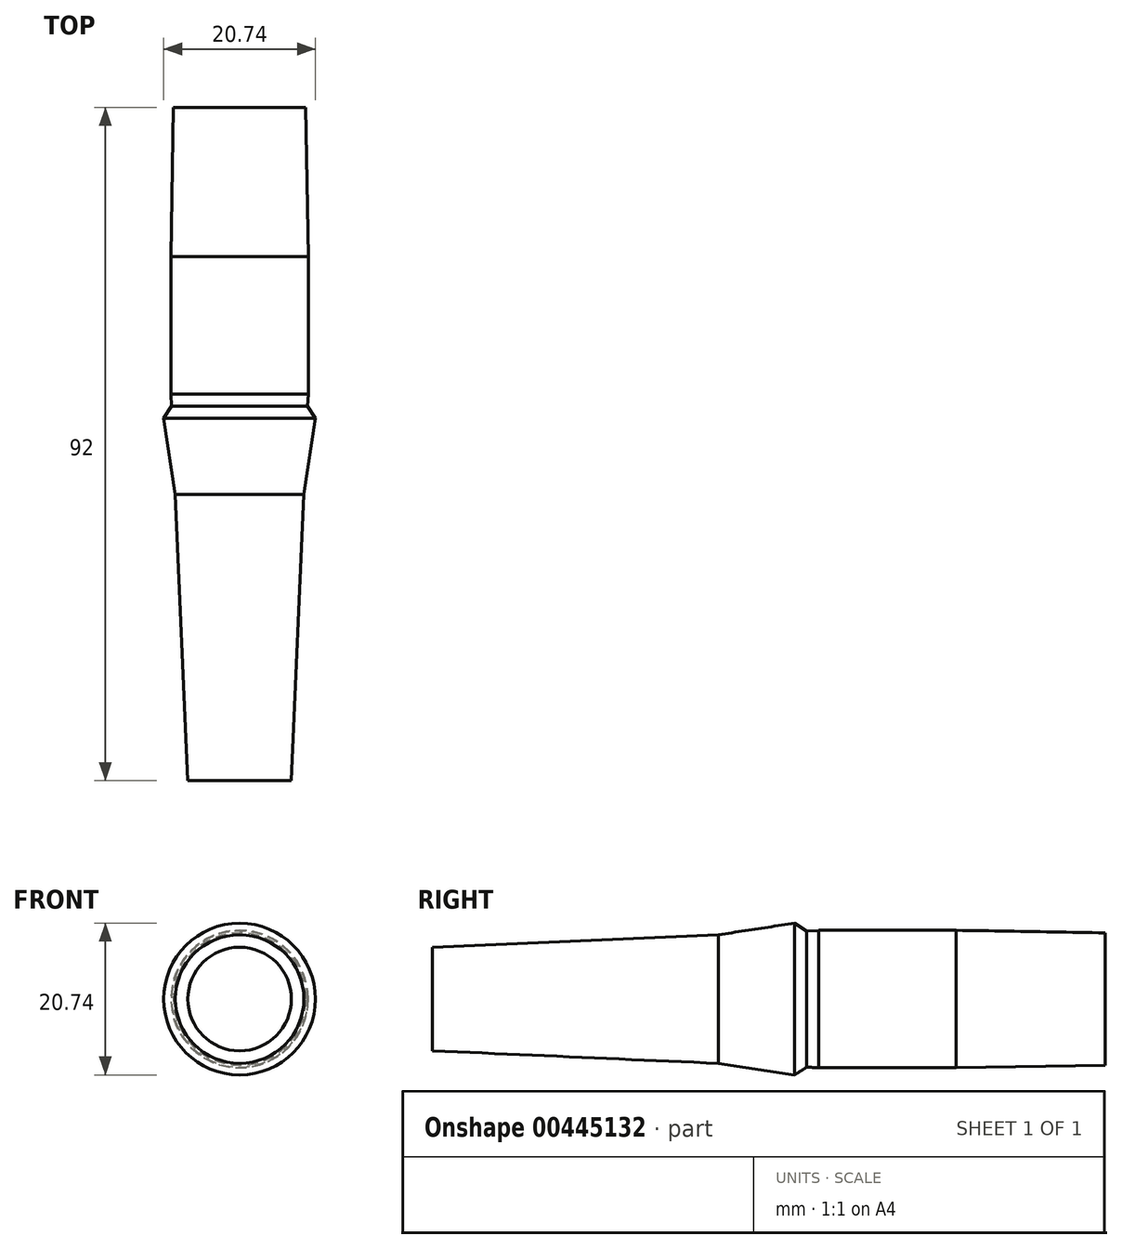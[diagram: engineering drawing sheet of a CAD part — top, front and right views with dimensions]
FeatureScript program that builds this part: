
annotation { "Feature Type Name" : "Feature", "Feature Type Description" : "" }
export const myFeature = defineFeature(function(context is Context, id is Id, definition is map)
    precondition{}
    {
        {
            var Q0;
            Q0=qCreatedBy(makeId("Front.planeOp"),FACE);
            var sketch = newSketch(context, id + "F0", { "sketchPlane" : qUnion([Q0])});
            skCircle(sketch, "E0", {"center": v(0, 0) * mm, "radius": 9.39 * mm});
            skSolve(sketch);
        }
        {
            var Q0;
            Q0=qSketchRegion(id+"F0",true);
            extrude(context, id + "F1", {"entities" : qUnion([Q0]), "depth" : 52.8 * mm, "hasDraft" : true, "draftAngle" : 2.5 * degree, "draftPullDirection" : true});
        }
        {
            var Q0;
            Q0=makeQuery(id+"F1.opExtrude","CAP_FACE",FACE,{"disambiguationData":[OSD([sQuery(id+"F0.wireOp",EDGE,"E0")])],"isStart":true});
            var sketch = newSketch(context, id + "F2", { "sketchPlane" : qUnion([Q0])});
            skCircle(sketch, "E1", {"center": v(0, 0) * mm, "radius": 9.4 * mm});
            skSolve(sketch);
        }
        {
            var Q0;
            Q0=qSketchRegion(id+"F2",true);
            extrude(context, id + "F3", {"entities" : qUnion([Q0]), "operationType" : NewBodyOperationType.ADD, "depth" : 18.8 * mm});
        }
        {
            var Q0;
            Q0=makeQuery(id+"F3.opExtrude","CAP_FACE",FACE,{"disambiguationData":[OSD([sQuery(id+"F2.wireOp",EDGE,"E1")])],"isStart":false});
            var sketch = newSketch(context, id + "F4", { "sketchPlane" : qUnion([Q0])});
            skCircle(sketch, "E2", {"center": v(0, 0) * mm, "radius": 9.4 * mm});
            skSolve(sketch);
        }
        {
            var Q0;
            Q0=qSketchRegion(id+"F4",true);
            extrude(context, id + "F5", {"entities" : qUnion([Q0]), "operationType" : NewBodyOperationType.ADD, "depth" : 20.4 * mm, "hasDraft" : true, "draftAngle" : 1 * degree, "draftPullDirection" : true});
        }
        {
            var Q0;
            Q0=qCreatedBy(makeId("Top.planeOp"),FACE);
            var sketch = newSketch(context, id + "F6", { "sketchPlane" : qUnion([Q0])});
            skLineSegment(sketch, "E3", {"start": v(-9.24, -1.5) * mm, "end": v(-10.37, -3.27) * mm});
            skLineSegment(sketch, "E4", {"start": v(-10.37, -3.27) * mm, "end": v(-8.7, -14.19) * mm});
            skLineSegment(sketch, "E5", {"start": v(-8.7, -14.19) * mm, "end": v(-9.24, -1.5) * mm});
            skSolve(sketch);
        }
        {
            var Q0;
            Q0=qSketchRegion(id+"F6",true);
            var Q1;
            Q1=makeQuery(id+"F1.opExtrude","CAP_EDGE",EDGE,{"disambiguationData":[OSD([sQuery(id+"F0.wireOp",EDGE,"E0")])],"isStart":false});
            revolve(context, id + "F7", {"operationType" : NewBodyOperationType.ADD, "entities" : qUnion([Q0]), "axis" : qUnion([Q1]), "revolveType" : RevolveType.FULL});
        }
    });
